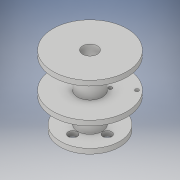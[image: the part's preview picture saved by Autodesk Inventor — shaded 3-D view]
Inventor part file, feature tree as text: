
AUTODESK INVENTOR PART (.ipt)
format: ipt  version: 2019 (Build 230136000, 136)  size: 157,184 bytes
history: native  units: in
note: dims shown in document units (in); Inventor stores cm internally (conversion verified against a paired STEP export)
features: sketch x4, hole x2, revolve x1, extrude x1
ambient origin geometry x8: Origin, YZ Plane, XZ Plane, XY Plane, X Axis, Y Axis, Z Axis, Center Point
bodies: Solid1 (feature_tree)
feature tree (8):
  revolve  "Revolution1"  [1 undecoded]
  extrude  "Extrusion1"  Depth=0.2756in
  hole  "Hole1"  [1 undecoded]
  hole  "Hole2"  [1 undecoded]
  sketch  "Sketch1"  dims[d1=0.2362in d2=0.3543in]
  sketch  "Sketch2"  dims[d3=0.0787in d4=0.2756in]
  sketch  "Sketch3"  dims[d5=0.0787in d6=0.3937in]
  sketch  "Sketch4"  dims[d7=0.0787in d8=0.0787in d9=1.1024in d10=0.4724in d11=0.3937in d17=1.0236in d18=0.0787in d19=90.0deg d20=0.1417in d21=0.2756in d22=1.5748in d24=360.0deg d26=0.0787in d27=0.0in d28=0.0591in d29=0.2362in d30=0.1575in d31=0.0787in d32=90.0deg d33=0.315in d34=0.0in d35=0.0591in d36=0.2362in d37=0.1575in d38=0.0787in d39=90.0deg d40=0.315in d41=0.0in]
note: 3 required parameter values undecoded (feature->parameter linkage not recoverable at this tier; creation-order binding heuristic only, values carry confidence <= 0.55)